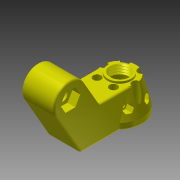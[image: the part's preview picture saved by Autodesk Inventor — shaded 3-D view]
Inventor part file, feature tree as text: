
AUTODESK INVENTOR PART (.ipt)
format: ipt  version: 2013 (Build 170138000, 138)  size: 448,000 bytes
history: native  units: mm
features: sketch x17, extrude x14, pattern_circular x2, loft x1, helix x1, fillet x1, projected_geometry x1
ambient origin geometry x8: Origin, YZ Plane, XZ Plane, XY Plane, X Axis, Y Axis, Z Axis, Center Point
bodies: Solid1 (feature_tree)
feature tree (37):
  extrude  "Extrusion1"  Depth=50.0mm
  extrude  "Extrusion2"  Depth=25.0mm
  extrude  "Extrusion11"  Depth=25.0mm TaperAngle=0.0deg
  extrude  "Extrusion27"  TaperAngle=120.0deg  [1 undecoded]
  loft  "Loft1"
  extrude  "Extrusion12"  Depth=19.0mm TaperAngle=0.0deg
  extrude  "Extrusion17"  Depth=1.5mm TaperAngle=0.0deg
  extrude  "Extrusion25"  Depth=10.0mm TaperAngle=0.0deg
  extrude  "Extrusion28"  Depth=5.0mm TaperAngle=0.0deg
  extrude  "Extrusion29"  TaperAngle=0.0deg  [1 undecoded]
  extrude  "Extrusion30"  TaperAngle=60.0deg  [1 undecoded]
  pattern_circular  "Circular Pattern1"  Count=6 Angle=360.0deg
  extrude  "Extrusion31"  Depth=12.5mm
  extrude  "Extrusion32"  Depth=14.5mm
  extrude  "Extrusion33"  Depth=5.0mm TaperAngle=0.0deg
  helix  "Coil2"  [1 undecoded]
  fillet  "Fillet4"  Radius=12.5mm
  extrude  "Extrusion34"  Depth=6.0mm
  pattern_circular  "Circular Pattern2"  [2 undecoded]
  sketch  "Sketch1"  dims[d0=8.1mm d2=50.0mm]
  sketch  "Sketch2"  dims[d3=14.0mm d4=25.0mm]
  sketch  "Sketch11"  dims[d6=25.0mm d7=25.0mm d8=0.0mm]
  sketch  "Sketch12"  dims[d9=25.0mm d10=0.0mm d40=120.0deg]
  sketch  "Sketch17"  dims[d53=13.1mm d54=6.0mm d55=0.0mm]
  sketch  "Sketch26"  dims[d56=16.2mm d58=19.0mm d59=0.0mm]
  sketch  "Sketch31"  dims[d77=18.0mm d80=1.5mm d81=0.0mm]
  sketch  "Sketch32"  dims[d120=13.9mm d122=10.0mm d123=0.0mm]
  sketch  "Sketch33"  dims[d128=35.0mm d130=5.0mm d131=0.0mm]
  sketch  "Sketch34"  dims[d132=0.0mm d133=90.0deg d134=0.0mm d135=90.0deg]
  sketch  "Sketch35"  dims[d136=5.0mm d137=-7.853982mm d138=60.0deg]
  sketch  "Sketch36"  dims[d139=12.5mm]
  sketch  "Sketch37"  dims[d140=3.2mm]
  sketch  "Sketch39"  dims[d141=5.0mm d142=0.0mm]
  sketch  "Sketch40"  dims[d143=6.0mm]
  sketch  "Sketch41"  dims[d145=5.0mm d146=0.0mm d147=60.0mm d148=360.0deg]
  sketch  "Sketch43"  dims[d150=3.2mm d152=12.5mm d153=14.5mm d154=5.0mm d155=0.0mm d156=14.5mm d158=12.5mm d159=6.0mm d160=5.0mm d161=0.0mm d162=5.6mm d163=2.5mm d164=10.0mm d165=0.0mm d166=0.0mm d167=2.0mm d168=2.0001mm d169=10.0mm d170=100.0mm d171=0.0mm d172=90.0deg d173=90.0deg d174=0.0mm d175=0.0mm d176=1.5mm d181=10.0mm d183=10.0mm d184=0.0mm d185=40.0mm d186=180.0deg]
  projected_geometry  "Project Cut Edges2"
note: 6 required parameter values undecoded (feature->parameter linkage not recoverable at this tier; creation-order binding heuristic only, values carry confidence <= 0.55)
